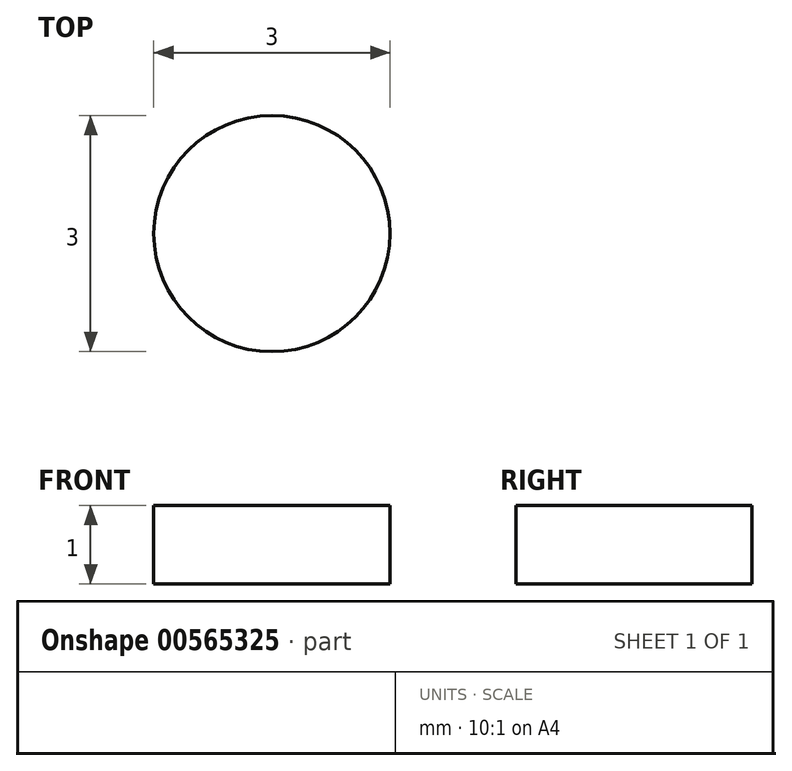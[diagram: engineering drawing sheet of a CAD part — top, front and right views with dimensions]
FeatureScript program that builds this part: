
annotation { "Feature Type Name" : "Feature", "Feature Type Description" : "" }
export const myFeature = defineFeature(function(context is Context, id is Id, definition is map)
    precondition{}
    {
        {
            var Q0;
            Q0=qCreatedBy(makeId("Top.planeOp"),FACE);
            var sketch = newSketch(context, id + "F0", { "sketchPlane" : qUnion([Q0])});
            skCircle(sketch, "E0", {"center": v(0, 0) * mm, "radius": 1.5 * mm});
            skSolve(sketch);
        }
        {
            var Q0;
            Q0=sQuery(id+"F0.wireOp",EDGE,"E0");
            extrude(context, id + "F1", {"bodyType" : ToolBodyType.SURFACE, "surfaceEntities" : qUnion([Q0]), "depth" : 1 * mm, "offsetDistance" : 25 * mm});
        }
    });
